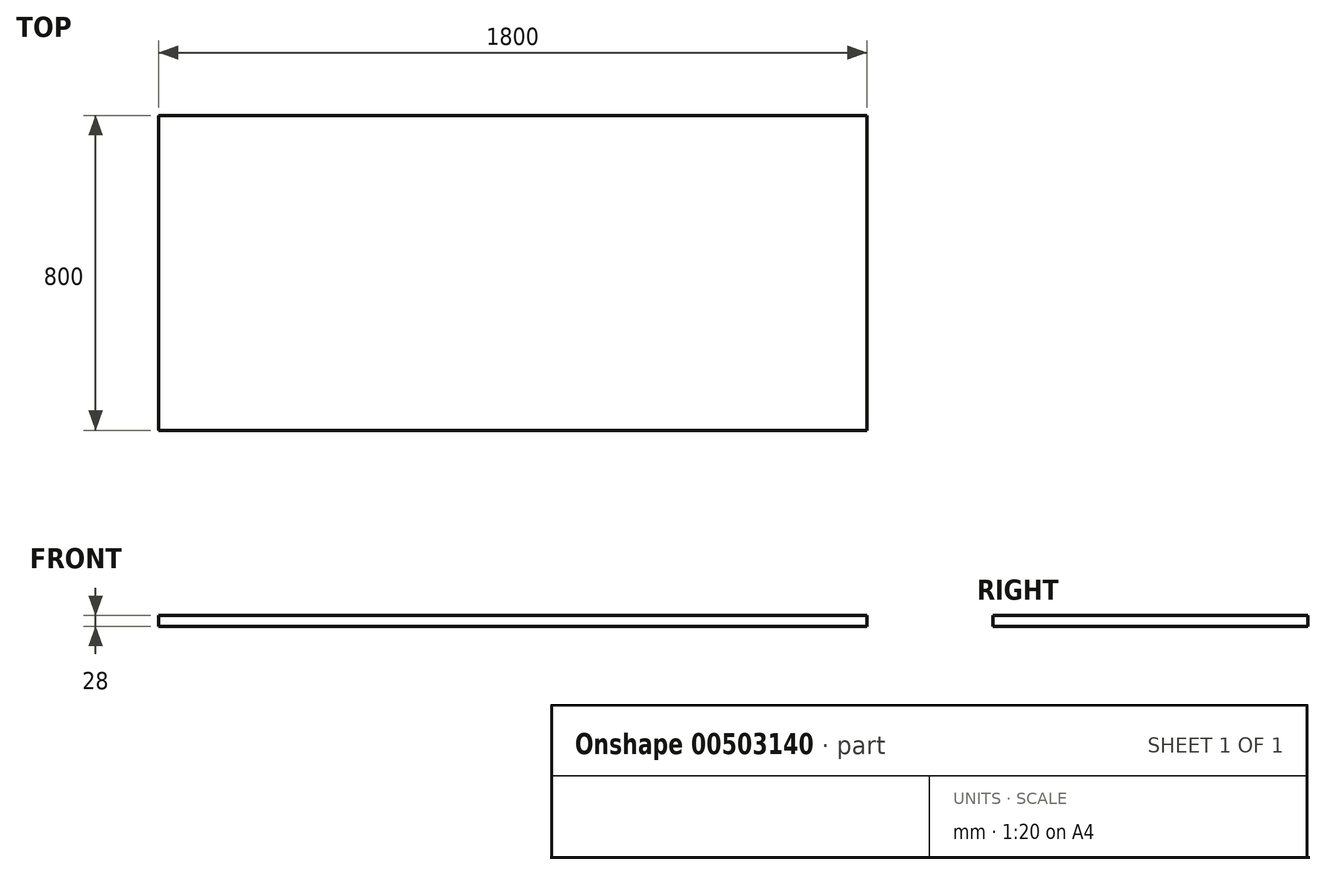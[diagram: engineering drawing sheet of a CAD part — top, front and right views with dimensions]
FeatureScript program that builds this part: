
annotation { "Feature Type Name" : "Feature", "Feature Type Description" : "" }
export const myFeature = defineFeature(function(context is Context, id is Id, definition is map)
    precondition{}
    {
        {
            var Q0;
            Q0=qCreatedBy(makeId("Top.planeOp"),FACE);
            var sketch = newSketch(context, id + "F0", { "sketchPlane" : qUnion([Q0])});
            skLineSegment(sketch, "E0.bottom", {"start": v(-600, -400) * mm, "end": v(1200, -400) * mm});
            skLineSegment(sketch, "E0.top", {"start": v(-600, 400) * mm, "end": v(1200, 400) * mm});
            skLineSegment(sketch, "E0.left", {"start": v(-600, -400) * mm, "end": v(-600, 400) * mm});
            skLineSegment(sketch, "E0.right", {"start": v(1200, -400) * mm, "end": v(1200, 400) * mm});
            skSolve(sketch);
        }
        {
            var Q0;
            Q0=qSketchRegion(id+"F0",true);
            extrude(context, id + "F1", {"entities" : qUnion([Q0]), "depth" : 28 * mm, "offsetDistance" : 25 * mm});
        }
        {
            var Q0;
            Q0=makeQuery(id+"F1.opExtrude","CAP_FACE",FACE,{"disambiguationData":[OSD([sQuery(id+"F0.wireOp",EDGE,"E0.bottom"),sQuery(id+"F0.wireOp",EDGE,"E0.top"),sQuery(id+"F0.wireOp",EDGE,"E0.left"),sQuery(id+"F0.wireOp",EDGE,"E0.right")])],"isStart":true});
            var sketch = newSketch(context, id + "F2", { "sketchPlane" : qUnion([Q0])});
            skLineSegment(sketch, "E1", {"start": v(-600, -300) * mm, "end": v(1200, -300) * mm, "construction": true});
            skSolve(sketch);
        }
    });
